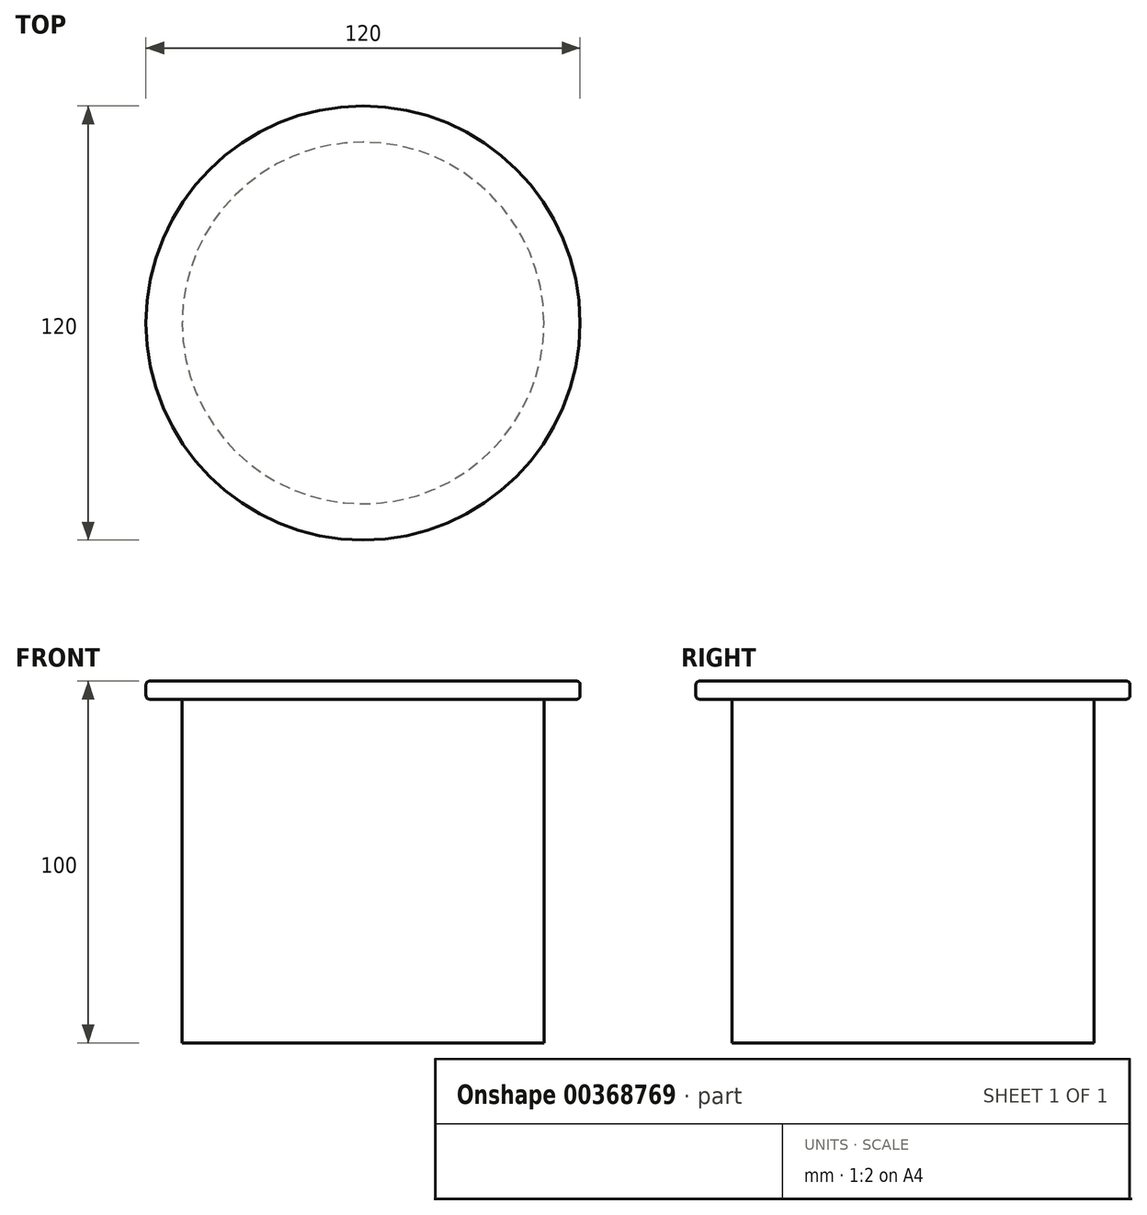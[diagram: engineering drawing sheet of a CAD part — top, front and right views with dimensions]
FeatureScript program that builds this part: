
annotation { "Feature Type Name" : "Feature", "Feature Type Description" : "" }
export const myFeature = defineFeature(function(context is Context, id is Id, definition is map)
    precondition{}
    {
        {
            var Q0;
            Q0=qCreatedBy(makeId("Top.planeOp"),FACE);
            var sketch = newSketch(context, id + "F0", { "sketchPlane" : qUnion([Q0])});
            skCircle(sketch, "E0", {"center": v(0, 0) * mm, "radius": 50 * mm});
            skSolve(sketch);
        }
        {
            var Q0;
            Q0=makeQuery(id+"F0.imprint","IMPRINT",FACE,{"disambiguationData":[TD([[makeQuery(id+"F0.imprint","IMPRINT",EDGE,{"derivedFrom":sQuery(id+"F0.wireOp",EDGE,"E0")}),1.0]])]});
            extrude(context, id + "F1", {"entities" : qUnion([Q0]), "depth" : 100 * mm});
        }
        {
            var Q0;
            Q0=makeQuery(id+"F1.opExtrude","CAP_FACE",FACE,{"disambiguationData":[OSD([sQuery(id+"F0.wireOp",EDGE,"E0")])],"isStart":false});
            var sketch = newSketch(context, id + "F2", { "sketchPlane" : qUnion([Q0])});
            skCircle(sketch, "E1.0", {"center": v(0, 0) * mm, "radius": 60 * mm});
            skSolve(sketch);
        }
        {
            var Q0;
            Q0 = qSketchRegion(id + "F2", true);
            extrude(context, id + "F3", {"entities" : qUnion([Q0]), "operationType" : NewBodyOperationType.ADD, "oppositeDirection" : true, "depth" : 5 * mm});
        }
        {
            var Q0;
            Q0=makeQuery(id+"F3.opExtrude","SWEPT_FACE",FACE,{"disambiguationData":[OSD([sQuery(id+"F2.wireOp",EDGE,"E1.0")])]});
            fillet(context, id + "F4", {"entities" : qUnion([Q0]), "radius" : 1 * mm, "tangentPropagation" : true, "allowEdgeOverflow" : false});
        }
    });
